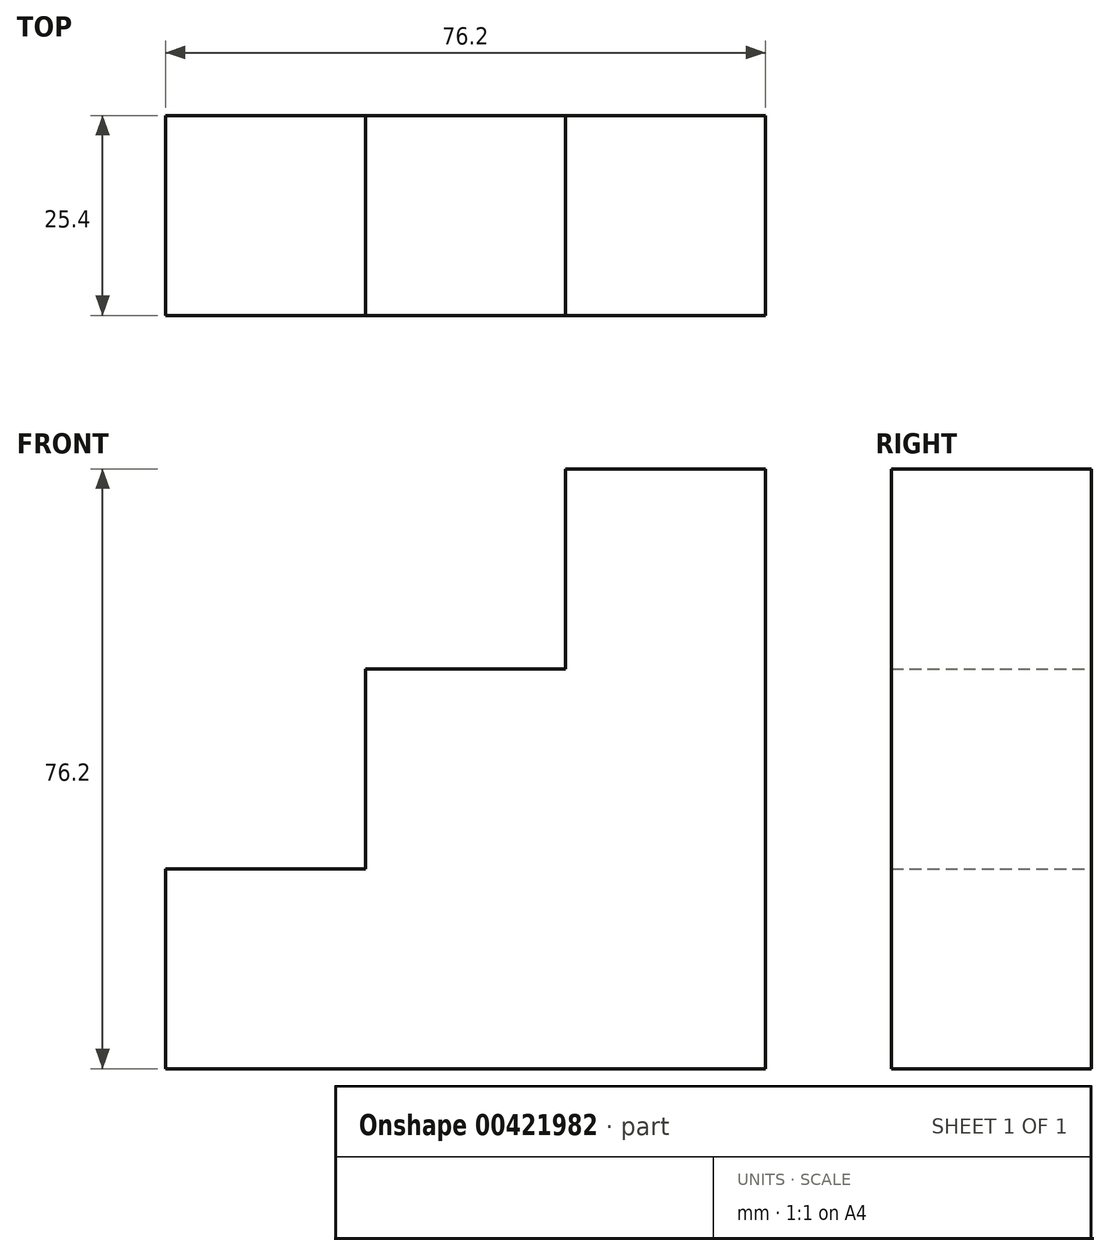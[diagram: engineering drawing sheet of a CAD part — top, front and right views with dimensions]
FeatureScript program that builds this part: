
annotation { "Feature Type Name" : "Feature", "Feature Type Description" : "" }
export const myFeature = defineFeature(function(context is Context, id is Id, definition is map)
    precondition{}
    {
        {
            var Q0;
            Q0=qCreatedBy(makeId("Front.planeOp"),FACE);
            var sketch = newSketch(context, id + "F0", { "sketchPlane" : qUnion([Q0])});
            skLineSegment(sketch, "E0", {"start": v(4.1, 0) * mm, "end": v(4.1, 76.2) * mm});
            skLineSegment(sketch, "E1", {"start": v(4.1, 76.2) * mm, "end": v(-21.3, 76.2) * mm});
            skLineSegment(sketch, "E2", {"start": v(-21.3, 76.2) * mm, "end": v(-21.3, 50.8) * mm});
            skLineSegment(sketch, "E3", {"start": v(-21.3, 50.8) * mm, "end": v(-46.7, 50.8) * mm});
            skLineSegment(sketch, "E4", {"start": v(-46.7, 50.8) * mm, "end": v(-46.7, 25.4) * mm});
            skLineSegment(sketch, "E5", {"start": v(-46.7, 25.4) * mm, "end": v(-72.1, 25.4) * mm});
            skLineSegment(sketch, "E6", {"start": v(-72.1, 25.4) * mm, "end": v(-72.1, 0) * mm});
            skLineSegment(sketch, "E7", {"start": v(-72.1, 0) * mm, "end": v(4.1, 0) * mm});
            skSolve(sketch);
        }
        {
            var Q0;
            Q0 = qSketchRegion(id + "F0", true);
            extrude(context, id + "F1", {"entities" : qUnion([Q0]), "depth" : 25.4 * mm});
        }
    });
